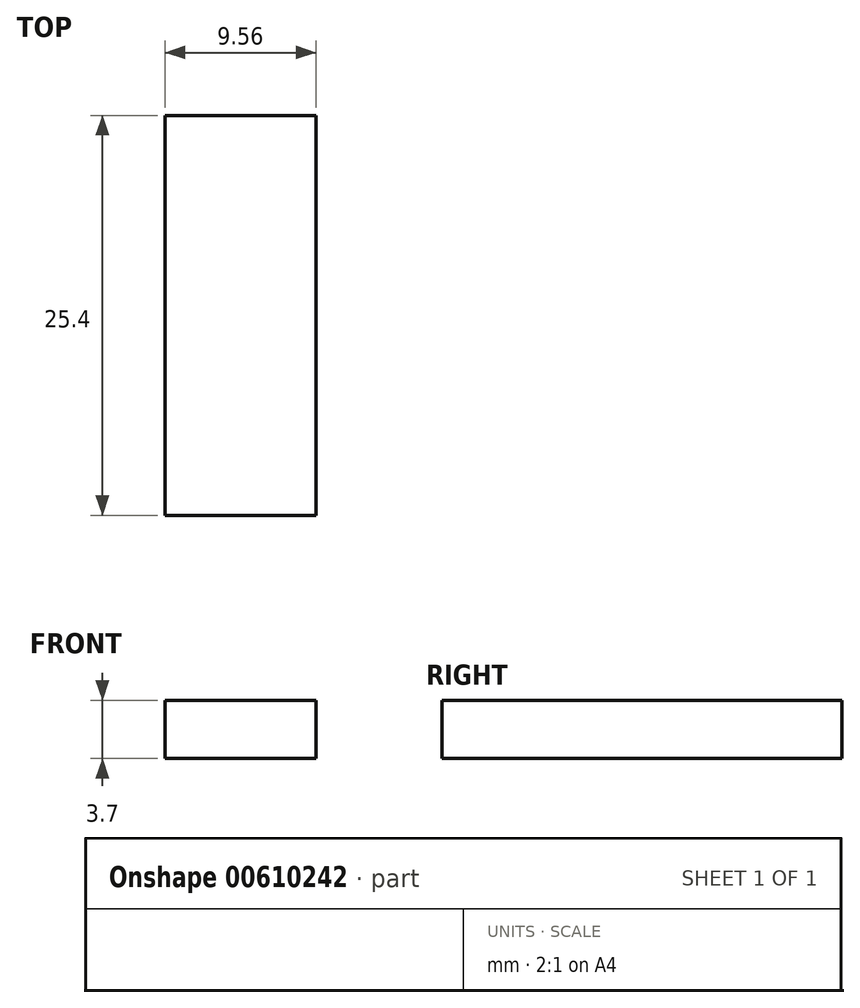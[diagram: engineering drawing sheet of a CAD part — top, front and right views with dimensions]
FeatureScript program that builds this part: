
annotation { "Feature Type Name" : "Feature", "Feature Type Description" : "" }
export const myFeature = defineFeature(function(context is Context, id is Id, definition is map)
    precondition{}
    {
        {
            var Q0;
            Q0=qCreatedBy(makeId("Front.planeOp"),FACE);
            var sketch = newSketch(context, id + "F0", { "sketchPlane" : qUnion([Q0])});
            skLineSegment(sketch, "E0.bottom", {"start": v(0, 0) * mm, "end": v(9.56, 0) * mm});
            skLineSegment(sketch, "E0.top", {"start": v(0, 3.7) * mm, "end": v(9.56, 3.7) * mm});
            skLineSegment(sketch, "E0.left", {"start": v(0, 0) * mm, "end": v(0, 3.7) * mm});
            skLineSegment(sketch, "E0.right", {"start": v(9.56, 0) * mm, "end": v(9.56, 3.7) * mm});
            skSolve(sketch);
        }
        {
            var Q0;
            Q0 = qSketchRegion(id + "F0", true);
            extrude(context, id + "F1", {"entities" : qUnion([Q0]), "depth" : 25.4 * mm, "offsetDistance" : 25.4 * mm});
        }
        {
            var Q0;
            Q0=qCreatedBy(makeId("Top.planeOp"),FACE);
            var sketch = newSketch(context, id + "F2", { "sketchPlane" : qUnion([Q0])});
            skCircle(sketch, "E1", {"center": v(4.7, -13.07) * mm, "radius": 2.75 * mm});
            skSolve(sketch);
        }
        {
            var Q0;
            Q0=sQuery(id+"F2.wireOp",EDGE,"E1");
            extrude(context, id + "F3", {"bodyType" : ToolBodyType.SURFACE, "surfaceEntities" : qUnion([Q0]), "depth" : 25.4 * mm, "offsetDistance" : 25.4 * mm});
        }
    });
